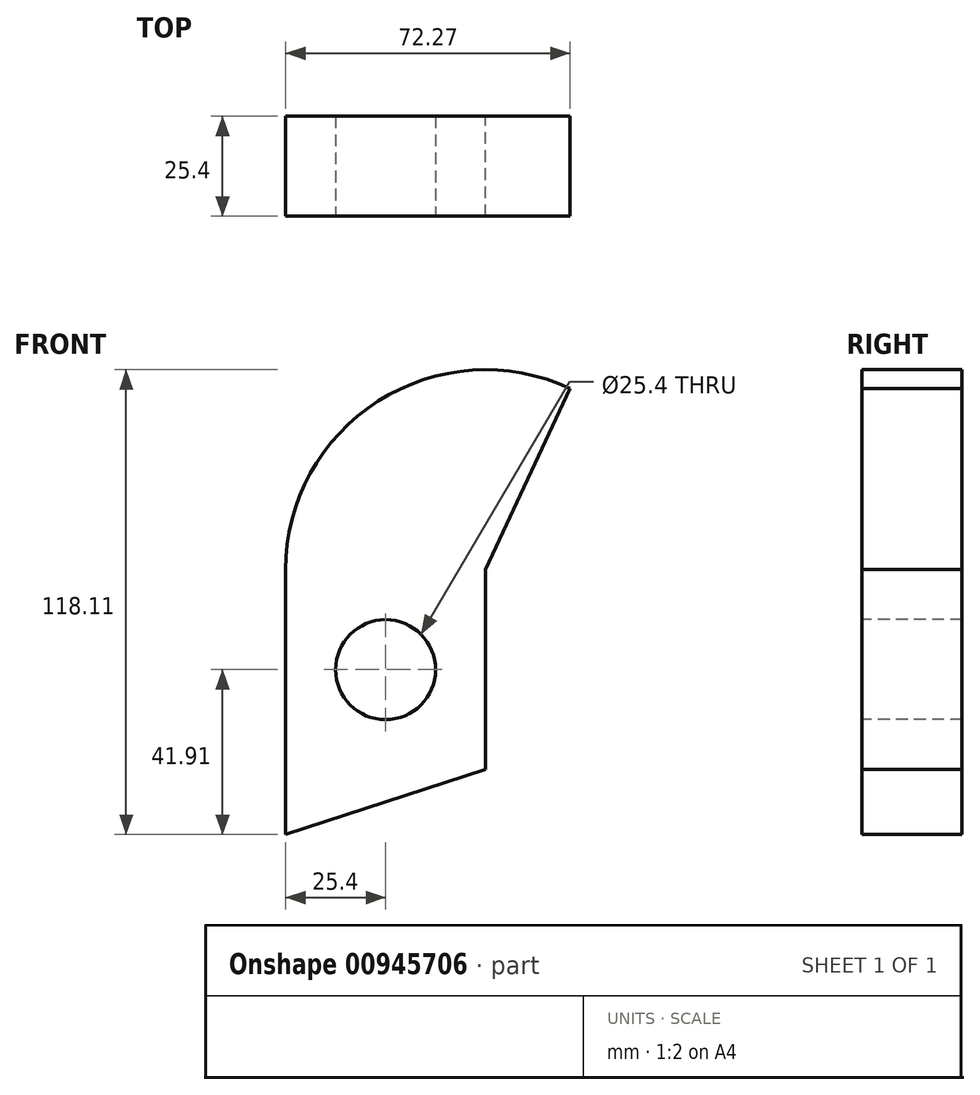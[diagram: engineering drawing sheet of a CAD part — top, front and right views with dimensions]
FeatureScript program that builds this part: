
annotation { "Feature Type Name" : "Feature", "Feature Type Description" : "" }
export const myFeature = defineFeature(function(context is Context, id is Id, definition is map)
    precondition{}
    {
        {
            var Q0;
            Q0=qCreatedBy(makeId("Front.planeOp"),FACE);
            var sketch = newSketch(context, id + "F0", { "sketchPlane" : qUnion([Q0])});
            skLineSegment(sketch, "E0", {"start": v(-50.8, 50.8) * mm, "end": v(-50.8, -16.5) * mm});
            skLineSegment(sketch, "E1", {"start": v(-50.8, -16.5) * mm, "end": v(0, 0) * mm});
            skLineSegment(sketch, "E2", {"start": v(0, 0) * mm, "end": v(0, 50.8) * mm});
            skLineSegment(sketch, "E3", {"start": v(0, 50.8) * mm, "end": v(-50.8, 50.8) * mm});
            skSolve(sketch);
        }
        {
            var Q0;
            Q0 = qSketchRegion(id + "F0", true);
            extrude(context, id + "F1", {"entities" : qUnion([Q0]), "depth" : 25.4 * mm, "offsetDistance" : 25.4 * mm});
        }
        {
            var Q0;
            Q0=makeQuery(id+"F1.opExtrude","CAP_FACE",FACE,{"disambiguationData":[OSD([sQuery(id+"F0.wireOp",EDGE,"E0"),sQuery(id+"F0.wireOp",EDGE,"E1"),sQuery(id+"F0.wireOp",EDGE,"E2"),sQuery(id+"F0.wireOp",EDGE,"E3")])],"isStart":false});
            var sketch = newSketch(context, id + "F2", { "sketchPlane" : qUnion([Q0])});
            skCircle(sketch, "E4", {"center": v(-25.4, 25.4) * mm, "radius": 12.7 * mm});
            skSolve(sketch);
        }
        {
            var Q0;
            Q0 = qSketchRegion(id + "F2", true);
            extrude(context, id + "F3", {"entities" : qUnion([Q0]), "operationType" : NewBodyOperationType.REMOVE, "endBound" : BoundingType.THROUGH_ALL, "oppositeDirection" : true, "depth" : 25.4 * mm, "offsetDistance" : 25.4 * mm});
        }
        {
            var Q0;
            Q0=makeQuery(id+"F1.opExtrude","SWEPT_FACE",FACE,{"disambiguationData":[OSD([sQuery(id+"F0.wireOp",EDGE,"E3")])]});
            var Q1;
            Q1=makeQuery(id+"F1.opExtrude","SWEPT_EDGE",EDGE,{"disambiguationData":[OSD([sQuery(id+"F0.wireOp",EDGE,"E2"),sQuery(id+"F0.wireOp",EDGE,"E3")])]});
            revolve(context, id + "F4", {"operationType" : NewBodyOperationType.ADD, "surfaceOperationType" : NewSurfaceOperationType.NEW, "entities" : qUnion([Q0]), "axis" : qUnion([Q1]), "revolveType" : RevolveType.ONE_DIRECTION, "angle" : 115 * degree});
        }
    });
